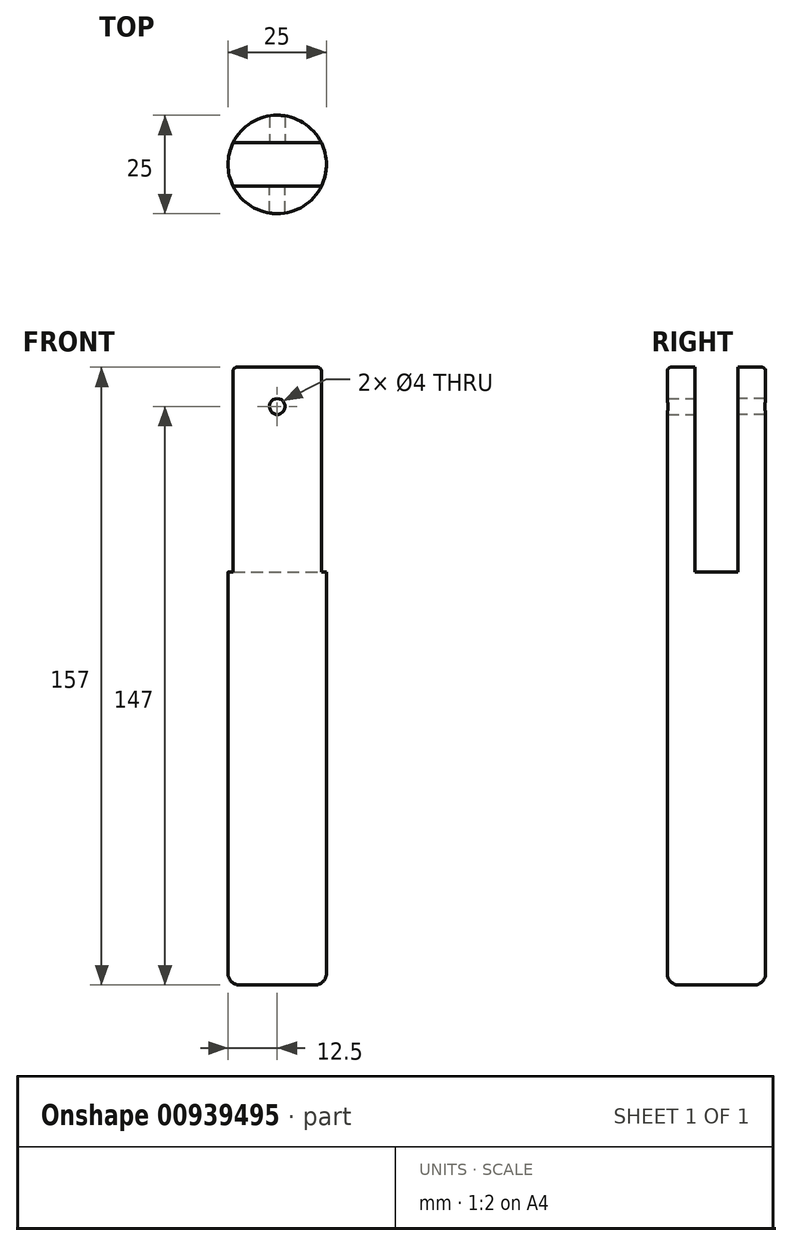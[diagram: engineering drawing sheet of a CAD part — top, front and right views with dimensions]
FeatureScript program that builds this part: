
annotation { "Feature Type Name" : "Feature", "Feature Type Description" : "" }
export const myFeature = defineFeature(function(context is Context, id is Id, definition is map)
    precondition{}
    {
        {
            var Q0;
            Q0=qCreatedBy(makeId("Top.planeOp"),FACE);
            var sketch = newSketch(context, id + "F0", { "sketchPlane" : qUnion([Q0])});
            skCircle(sketch, "E0", {"center": v(0, 0) * mm, "radius": 12.5 * mm});
            skSolve(sketch);
        }
        {
            var Q0;
            Q0=qSketchRegion(id+"F0",true);
            extrude(context, id + "F1", {"entities" : qUnion([Q0]), "depth" : 105 * mm, "offsetDistance" : 25 * mm});
        }
        {
            var Q0;
            Q0=makeQuery(id+"F1.opExtrude","CAP_FACE",FACE,{"disambiguationData":[OSD([sQuery(id+"F0.wireOp",EDGE,"E0")])],"isStart":false});
            var sketch = newSketch(context, id + "F2", { "sketchPlane" : qUnion([Q0])});
            skLineSegment(sketch, "E1", {"start": v(-11.22, 5.52) * mm, "end": v(11.22, 5.52) * mm});
            skLineSegment(sketch, "E2", {"start": v(-11.23, -5.48) * mm, "end": v(11.23, -5.48) * mm});
            skSolve(sketch);
        }
        {
            var Q0;
            {var subQ0=sQuery(id+"F2.wireOp",EDGE,"E2");Q0=makeQuery(id+"F2.imprint","IMPRINT",FACE,{"disambiguationData":[TD([[makeQuery(id+"F2.imprint","IMPRINT",EDGE,{"derivedFrom":subQ0}),-1.0]])]});}
            var Q1;
            {var subQ0=sQuery(id+"F2.wireOp",EDGE,"E1");Q1=makeQuery(id+"F2.imprint","IMPRINT",FACE,{"disambiguationData":[TD([[makeQuery(id+"F2.imprint","IMPRINT",EDGE,{"derivedFrom":subQ0}),1.0]])]});}
            extrude(context, id + "F3", {"entities" : qUnion([Q0, Q1]), "operationType" : NewBodyOperationType.ADD, "depth" : 52 * mm, "offsetDistance" : 25 * mm});
        }
        {
            var Q0;
            Q0=makeQuery(id+"F1.opExtrude","CAP_EDGE",EDGE,{"disambiguationData":[OSD([sQuery(id+"F0.wireOp",EDGE,"E0")])],"isStart":true});
            fillet(context, id + "F4", {"entities" : qUnion([Q0]), "radius" : 3 * mm, "tangentPropagation" : true, "allowEdgeOverflow" : false});
        }
        {
            var Q0;
            Q0=makeQuery(id+"F3.opExtrude","SWEPT_FACE",FACE,{"disambiguationData":[OSD([sQuery(id+"F2.wireOp",EDGE,"E1")])]});
            var sketch = newSketch(context, id + "F5", { "sketchPlane" : qUnion([Q0])});
            skPoint(sketch, "E3", {"position": v(0, 147) * mm});
            skPoint(sketch, "E3.positionSnap0", {"position": v(0, 157) * mm});
            skSolve(sketch);
        }
        {
            var Q0;
            Q0=sQuery(id+"F5.wireOp",VERTEX,"E3");
            var Q1;
            Q1=makeQuery(id+"F1.opExtrude","SWEPT_BODY",BODY,{"disambiguationData":[OSD([sQuery(id+"F0.wireOp",EDGE,"E0")])]});
            hole(context, id + "F6", {"style" : HoleStyle.SIMPLE, "endStyle" : HoleEndStyle.BLIND, "holeDiameter" : 4 * mm, "majorDiameter" : 5 * mm, "holeDepth" : 20 * mm, "isTappedThrough" : true, "tappedDepth" : 12 * mm, "tapClearance" : 3, "locations" : qUnion([Q0]), "scope" : qUnion([Q1])});
        }
        {
            var Q0;
            Q0=sQuery(id+"F5.wireOp",VERTEX,"E3");
            var Q1;
            Q1=makeQuery(id+"F1.opExtrude","SWEPT_BODY",BODY,{"disambiguationData":[OSD([sQuery(id+"F0.wireOp",EDGE,"E0")])]});
            hole(context, id + "F7", {"style" : HoleStyle.SIMPLE, "endStyle" : HoleEndStyle.BLIND, "oppositeDirection" : true, "holeDiameter" : 4 * mm, "majorDiameter" : 5 * mm, "holeDepth" : 20 * mm, "isTappedThrough" : true, "tappedDepth" : 12 * mm, "tapClearance" : 3, "locations" : qUnion([Q0]), "scope" : qUnion([Q1])});
        }
        {
            var Q0;
            {var subQ0=sQuery(id+"F2.wireOp",EDGE,"E1");var subQ1=sQuery(id+"F0.wireOp",EDGE,"E0");var subQ2=makeQuery(id+"F1.opExtrude","CAP_EDGE",EDGE,{"disambiguationData":[OSD([subQ1])],"isStart":false});Q0=makeQuery(id+"F3.opExtrude","CAP_EDGE",EDGE,{"disambiguationData":[OSD([subQ1]),TDD([makeQuery(id+"F2.imprint","IMPRINT",EDGE,{"disambiguationData":[TD([[makeQuery(id+"F2.imprint","INTERSECT",VERTEX,{"disambiguationData":[OD(0.0)],"derivedFrom":[subQ2,subQ0]}),1.0]])],"derivedFrom":subQ2})])],"isStart":false});}
            var Q1;
            {var subQ0=sQuery(id+"F2.wireOp",EDGE,"E2");var subQ1=sQuery(id+"F0.wireOp",EDGE,"E0");var subQ2=makeQuery(id+"F1.opExtrude","CAP_EDGE",EDGE,{"disambiguationData":[OSD([subQ1])],"isStart":false});Q1=makeQuery(id+"F3.opExtrude","CAP_EDGE",EDGE,{"disambiguationData":[OSD([subQ1]),TDD([makeQuery(id+"F2.imprint","IMPRINT",EDGE,{"disambiguationData":[TD([[makeQuery(id+"F2.imprint","INTERSECT",VERTEX,{"disambiguationData":[OD(0.0)],"derivedFrom":[subQ2,subQ0]}),-1.0]])],"derivedFrom":subQ2})])],"isStart":false});}
            fillet(context, id + "F8", {"entities" : qUnion([Q0, Q1]), "radius" : 1 * mm, "tangentPropagation" : true, "allowEdgeOverflow" : false});
        }
    });
